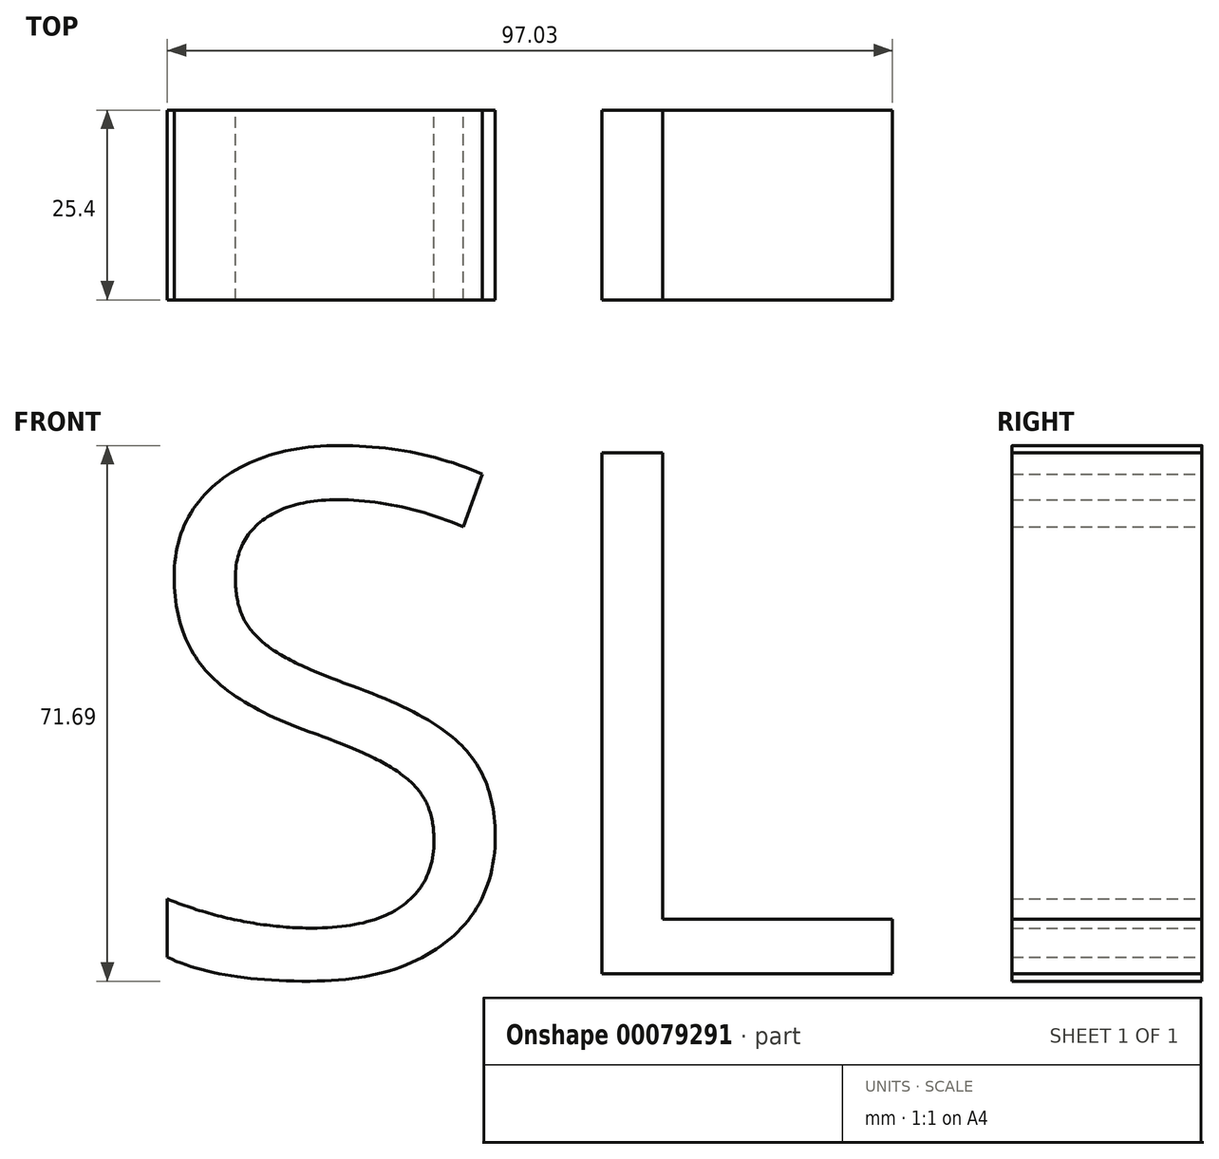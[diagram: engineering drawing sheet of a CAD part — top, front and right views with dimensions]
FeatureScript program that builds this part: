
annotation { "Feature Type Name" : "Feature", "Feature Type Description" : "" }
export const myFeature = defineFeature(function(context is Context, id is Id, definition is map)
    precondition{}
    {
        {
            var Q0;
            Q0=qCreatedBy(makeId("Front.planeOp"),FACE);
            var sketch = newSketch(context, id + "F0", { "sketchPlane" : qUnion([Q0])});
            skText(sketch, "E0", { "text": "SL\n", "fontName": "OpenSans-Regular.ttf"});
            const initialGuessF0  = {"E0": [-0.05385, -0.03992, 1, 0, 0.07033]};
            skSetInitialGuess(sketch, initialGuessF0);
            skSolve(sketch);
        }
        {
            var Q0;
            Q0 = qSketchRegion(id + "F0", true);
            extrude(context, id + "F1", {"entities" : qUnion([Q0]), "depth" : 25.4 * mm});
        }
    });
